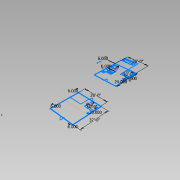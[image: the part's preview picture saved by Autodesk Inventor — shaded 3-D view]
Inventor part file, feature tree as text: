
AUTODESK INVENTOR PART (.ipt)
format: ipt  version: 2014 (Build 180170000, 170)  size: 772,608 bytes
history: native  units: in
note: dims shown in document units (in); Inventor stores cm internally (conversion verified against a paired STEP export)
features: other x36, sketch x1
ambient origin geometry x8: Origin, YZ Plane, XZ Plane, XY Plane, X Axis, Y Axis, Z Axis, Center Point
feature tree (37):
  other  "Blocks"
  sketch  "Sketch1"  dims[d35=336.0in d36=384.0in d48=11.0in d62=11.0in d67=120.0in d68=96.0in d69=20.0in d71=3.1496in d73=0.3937in d75=0.7874in d77=0.3937in d79=1.1811in d81=0.3937in d83=3.1496in d85=0.3937in d91=1.1811in d93=0.3937in d94=1.0in d96=1.0in d104=6.0in d105=6.0in d106=6.0in d107=336.0in d108=384.0in d109=6.0in d112=144.0in d115=120.0in d150=6.0in d151=24.0in d152=24.0in d153=30.0in d154=24.0in]
  other  "DOOR"
  other  "Block2"
  other  "Block3"
  other  "Block4"
  other  "Block5"
  other  "Block6"
  other  "Block7"
  other  "Block8"
  other  "Block9"
  other  "Block10"
  other  "Block11"
  other  "Block12"
  other  "Block13"
  other  "Block14"
  other  "Block15"
  other  "Block16"
  other  "fridge"
  other  "DOOR:2"
  other  "Block6:1"
  other  "Block7:2"
  other  "Block8:1"
  other  "Block8:4"
  other  "Block8:5"
  other  "Block9:1"
  other  "Block10:1"
  other  "Block7:3"
  other  "Block12:1"
  other  "Block13:1"
  other  "Block4:3"
  other  "Block14:1"
  other  "Block8:6"
  other  "Block10:2"
  other  "Block15:1"
  other  "Block16:1"
  other  "fridge:1"
